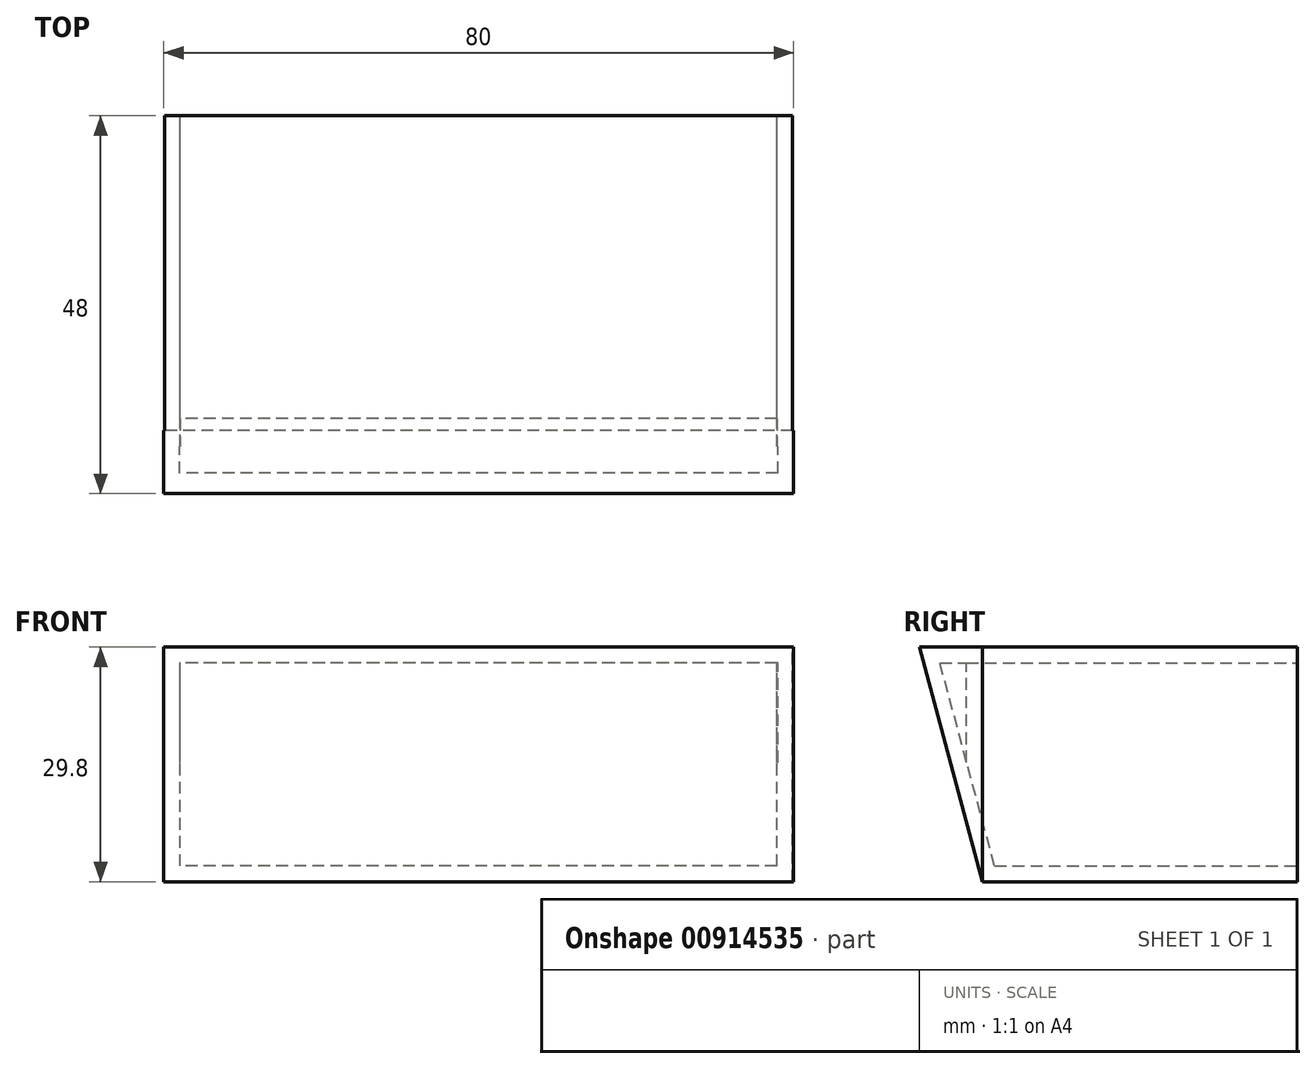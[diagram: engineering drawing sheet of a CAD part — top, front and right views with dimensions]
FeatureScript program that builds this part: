
annotation { "Feature Type Name" : "Feature", "Feature Type Description" : "" }
export const myFeature = defineFeature(function(context is Context, id is Id, definition is map)
    precondition{}
    {
        {
            var Q0;
            Q0=qCreatedBy(makeId("Front.planeOp"),FACE);
            var sketch = newSketch(context, id + "F0", { "sketchPlane" : qUnion([Q0])});
            skLineSegment(sketch, "E0.bottom", {"start": v(39.9, -14.9) * mm, "end": v(-39.9, -14.9) * mm});
            skLineSegment(sketch, "E0.top", {"start": v(39.9, 14.9) * mm, "end": v(-39.9, 14.9) * mm});
            skLineSegment(sketch, "E0.left", {"start": v(39.9, -14.9) * mm, "end": v(39.9, 14.9) * mm});
            skLineSegment(sketch, "E0.right", {"start": v(-39.9, -14.9) * mm, "end": v(-39.9, 14.9) * mm});
            skPoint(sketch, "E0.middle", {"position": v(0, 0) * mm});
            skSolve(sketch);
        }
        {
            var Q0;
            Q0=makeQuery(id+"F0.imprint","IMPRINT",FACE,{"disambiguationData":[TD([[makeQuery(id+"F0.imprint","IMPRINT",EDGE,{"derivedFrom":sQuery(id+"F0.wireOp",EDGE,"E0.bottom")}),-1.0]])]});
            extrude(context, id + "F1", {"entities" : qUnion([Q0]), "endBound" : BoundingType.SYMMETRIC, "depth" : 40 * mm, "offsetDistance" : 25 * mm, "hasSecondDirection" : true, "secondDirectionOppositeDirection" : true, "secondDirectionDepth" : 25 * mm});
        }
        {
            var Q0;
            Q0=qCreatedBy(makeId("Right.planeOp"),FACE);
            var sketch = newSketch(context, id + "F2", { "sketchPlane" : qUnion([Q0])});
            skLineSegment(sketch, "E1", {"start": v(-20, -14.9) * mm, "end": v(-28, 14.9) * mm});
            skLineSegment(sketch, "E2", {"start": v(-28, 14.9) * mm, "end": v(-20, 14.9) * mm});
            skLineSegment(sketch, "E3", {"start": v(-20, 14.9) * mm, "end": v(-20, -14.9) * mm});
            skSolve(sketch);
        }
        {
            var Q0;
            Q0=makeQuery(id+"F2.imprint","IMPRINT",FACE,{"disambiguationData":[TD([[makeQuery(id+"F2.imprint","IMPRINT",EDGE,{"derivedFrom":sQuery(id+"F2.wireOp",EDGE,"E1")}),-1.0]])]});
            extrude(context, id + "F3", {"entities" : qUnion([Q0]), "operationType" : NewBodyOperationType.ADD, "endBound" : BoundingType.SYMMETRIC, "depth" : 80 * mm, "offsetDistance" : 25 * mm});
        }
        {
            var Q0;
            Q0=makeQuery(id+"F1.opExtrude","CAP_FACE",FACE,{"disambiguationData":[OSD([sQuery(id+"F0.wireOp",EDGE,"E0.bottom"),sQuery(id+"F0.wireOp",EDGE,"E0.top"),sQuery(id+"F0.wireOp",EDGE,"E0.left"),sQuery(id+"F0.wireOp",EDGE,"E0.right")])],"isStart":true});
            shell(context, id + "F4", {"entities" : qUnion([Q0]), "thickness" : 2 * mm});
        }
    });
